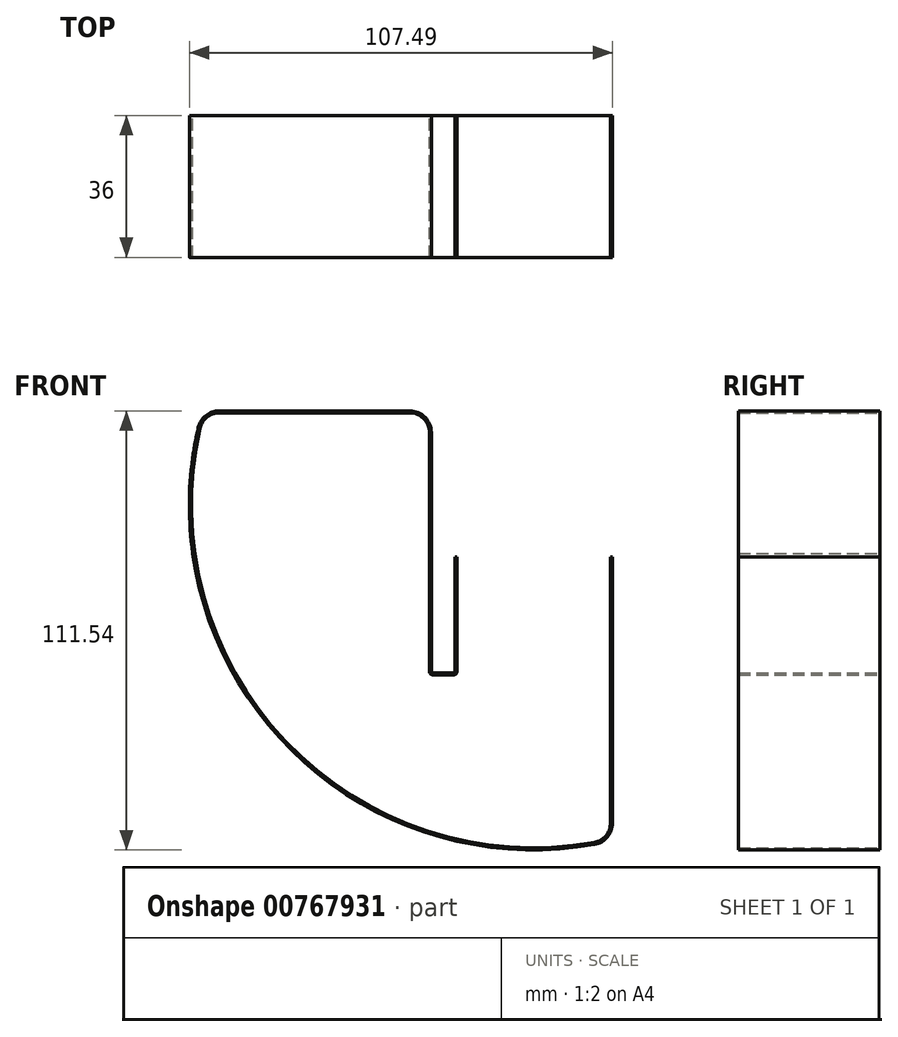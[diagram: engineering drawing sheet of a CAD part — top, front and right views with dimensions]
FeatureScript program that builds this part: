
annotation { "Feature Type Name" : "Feature", "Feature Type Description" : "" }
export const myFeature = defineFeature(function(context is Context, id is Id, definition is map)
    precondition{}
    {
        {
            var Q0;
            Q0=qCreatedBy(makeId("Front.planeOp"),FACE);
            var sketch = newSketch(context, id + "F0", { "sketchPlane" : qUnion([Q0])});
            skLineSegment(sketch, "E0", {"start": v(19.5, -13.15) * mm, "end": v(20, -13.15) * mm});
            skLineSegment(sketch, "E1", {"start": v(-19.5, -13.15) * mm, "end": v(-20, -13.15) * mm});
            skLineSegment(sketch, "E2", {"start": v(-20, -13.15) * mm, "end": v(-20, -23.15) * mm});
            skLineSegment(sketch, "E3.0", {"start": v(-31.5, 23.5) * mm, "end": v(-50.68, 23.5) * mm});
            skArc(sketch, "E4", {"start": v(-85.23, 19.74) * mm, "mid": v(-86.02, 15.96) * mm, "end": v(-86.64, 12.14) * mm});
            skLineSegment(sketch, "E5", {"start": v(-31.5, 24) * mm, "end": v(-50.68, 24) * mm});
            skArc(sketch, "E6.0", {"start": v(-84.74, 19.63) * mm, "mid": v(-85.53, 15.87) * mm, "end": v(-86.14, 12.07) * mm});
            skLineSegment(sketch, "E7", {"start": v(20, -13.15) * mm, "end": v(20, -23.15) * mm});
            skLineSegment(sketch, "E8", {"start": v(-25.5, -42.65) * mm, "end": v(-20.5, -42.65) * mm});
            skLineSegment(sketch, "E9", {"start": v(-20.5, -43.15) * mm, "end": v(-25.5, -43.15) * mm});
            skLineSegment(sketch, "E10", {"start": v(-26.5, 18.5) * mm, "end": v(-26.5, 5) * mm});
            skLineSegment(sketch, "E11", {"start": v(-26, 18.5) * mm, "end": v(-26, 5) * mm});
            skPoint(sketch, "E12.visualSharp", {"position": v(19.5, -84.82) * mm});
            skArc(sketch, "E12.filletArc", {"start": v(15.38, -85.67) * mm, "mid": v(18.34, -83.95) * mm, "end": v(19.5, -80.74) * mm});
            skPoint(sketch, "E13.visualSharp", {"position": v(20, -85.22) * mm});
            skArc(sketch, "E13.filletArc", {"start": v(15.47, -86.16) * mm, "mid": v(18.72, -84.27) * mm, "end": v(20, -80.74) * mm});
            skPoint(sketch, "E14.visualSharp", {"position": v(-83.75, 23.5) * mm});
            skArc(sketch, "E14.filletArc", {"start": v(-79.87, 23.5) * mm, "mid": v(-82.98, 22.41) * mm, "end": v(-84.74, 19.63) * mm});
            skPoint(sketch, "E15.visualSharp", {"position": v(-84.13, 24) * mm});
            skArc(sketch, "E15.filletArc", {"start": v(-79.87, 24) * mm, "mid": v(-83.3, 22.8) * mm, "end": v(-85.23, 19.74) * mm});
            skPoint(sketch, "E16.visualSharp", {"position": v(-26.5, 23.5) * mm});
            skArc(sketch, "E16.filletArc", {"start": v(-26.5, 18.5) * mm, "mid": v(-27.96, 22.04) * mm, "end": v(-31.5, 23.5) * mm});
            skArc(sketch, "E17.filletArc", {"start": v(-26, 18.5) * mm, "mid": v(-27.61, 22.39) * mm, "end": v(-31.5, 24) * mm});
            skPoint(sketch, "E18.visualSharp", {"position": v(-26, -42.65) * mm});
            skArc(sketch, "E18.filletArc", {"start": v(-26, -42.15) * mm, "mid": v(-25.85, -42.5) * mm, "end": v(-25.5, -42.65) * mm});
            skPoint(sketch, "E19.visualSharp", {"position": v(-20, -42.65) * mm});
            skArc(sketch, "E19.filletArc", {"start": v(-20.5, -42.65) * mm, "mid": v(-20.15, -42.5) * mm, "end": v(-20, -42.15) * mm});
            skPoint(sketch, "E20.visualSharp", {"position": v(-19.5, -43.15) * mm});
            skArc(sketch, "E20.filletArc", {"start": v(-20.5, -43.15) * mm, "mid": v(-19.8, -42.86) * mm, "end": v(-19.5, -42.15) * mm});
            skPoint(sketch, "E21.visualSharp", {"position": v(-26.5, -43.15) * mm});
            skArc(sketch, "E21.filletArc", {"start": v(-26.5, -42.15) * mm, "mid": v(-26.2, -42.86) * mm, "end": v(-25.5, -43.15) * mm});
            skLineSegment(sketch, "E22.direction2", {"start": v(19.5, -42.15) * mm, "end": v(19.5, -58.15) * mm, "construction": true});
            skLineSegment(sketch, "E23.trimOffspring", {"start": v(20, -33.15) * mm, "end": v(20, -58.15) * mm});
            skLineSegment(sketch, "E24.trimOffspring", {"start": v(19.5, -42.15) * mm, "end": v(19.5, -58.15) * mm});
            skLineSegment(sketch, "E25.trimOffspring", {"start": v(20, -68.15) * mm, "end": v(20, -80.74) * mm});
            skLineSegment(sketch, "E26.trimOffspring", {"start": v(19.5, -68.15) * mm, "end": v(19.5, -80.74) * mm});
            skLineSegment(sketch, "E27.trimOffspring", {"start": v(-20, -33.15) * mm, "end": v(-20, -42.15) * mm});
            skLineSegment(sketch, "E28.trimOffspring", {"start": v(-26, -33.15) * mm, "end": v(-26, -42.15) * mm});
            skLineSegment(sketch, "E29.trimOffspring", {"start": v(-26.5, -33.15) * mm, "end": v(-26.5, -42.15) * mm});
            skLineSegment(sketch, "E30.trimOffspring", {"start": v(-26, -5) * mm, "end": v(-26, -23.15) * mm});
            skLineSegment(sketch, "E31.trimOffspring", {"start": v(-26.5, -5) * mm, "end": v(-26.5, -23.15) * mm});
            skLineSegment(sketch, "E32.trimOffspring", {"start": v(-60.68, 23.5) * mm, "end": v(-79.87, 23.5) * mm});
            skLineSegment(sketch, "E33.trimOffspring", {"start": v(-60.68, 24) * mm, "end": v(-79.87, 24) * mm});
            skLineSegment(sketch, "E34.1.1", {"start": v(-86.63, -12.2) * mm, "end": v(-86.64, -12.2) * mm});
            skArc(sketch, "E35.trimOffspring", {"start": v(-52.35, -69.52) * mm, "mid": v(-33.28, -80.42) * mm, "end": v(-12.08, -86.2) * mm});
            skArc(sketch, "E36.trimOffspring", {"start": v(-52.65, -69.92) * mm, "mid": v(-33.47, -80.88) * mm, "end": v(-12.15, -86.69) * mm});
            skArc(sketch, "E37.trimOffspring", {"start": v(12.14, -86.19) * mm, "mid": v(13.76, -85.94) * mm, "end": v(15.38, -85.67) * mm});
            skArc(sketch, "E38.trimOffspring", {"start": v(12.21, -86.68) * mm, "mid": v(13.84, -86.43) * mm, "end": v(15.47, -86.16) * mm});
            skArc(sketch, "E39.trimOffspring", {"start": v(-86.64, -12.2) * mm, "mid": v(-80.83, -33.52) * mm, "end": v(-69.87, -52.7) * mm});
            skArc(sketch, "E40.trimOffspring", {"start": v(-86.15, -12.14) * mm, "mid": v(-80.37, -33.33) * mm, "end": v(-69.47, -52.4) * mm});
            skLineSegment(sketch, "E41", {"start": v(19.5, -33.15) * mm, "end": v(19.5, -23.15) * mm});
            skLineSegment(sketch, "E42", {"start": v(-19.5, -33.15) * mm, "end": v(-19.5, -23.15) * mm});
            skArc(sketch, "E43", {"start": v(-86.64, 12.14) * mm, "mid": v(-87.49, -0.03) * mm, "end": v(-86.63, -12.2) * mm});
            skArc(sketch, "E44", {"start": v(-69.87, -52.7) * mm, "mid": v(-61.86, -61.9) * mm, "end": v(-52.65, -69.92) * mm});
            skArc(sketch, "E45", {"start": v(12.21, -86.68) * mm, "mid": v(0.03, -87.54) * mm, "end": v(-12.15, -86.69) * mm});
            skArc(sketch, "E46", {"start": v(-12.08, -86.2) * mm, "mid": v(0.03, -87.04) * mm, "end": v(12.14, -86.19) * mm});
            skArc(sketch, "E47", {"start": v(-52.35, -69.52) * mm, "mid": v(-61.5, -61.55) * mm, "end": v(-69.47, -52.4) * mm});
            skArc(sketch, "E48", {"start": v(-86.15, -12.14) * mm, "mid": v(-87, -0.03) * mm, "end": v(-86.14, 12.07) * mm});
            skLineSegment(sketch, "E49", {"start": v(-60.68, 24) * mm, "end": v(-50.68, 24) * mm});
            skLineSegment(sketch, "E50", {"start": v(-50.68, 23.5) * mm, "end": v(-60.68, 23.5) * mm});
            skLineSegment(sketch, "E51", {"start": v(-26.5, 5) * mm, "end": v(-26.5, -5) * mm});
            skLineSegment(sketch, "E52", {"start": v(-26, -5) * mm, "end": v(-26, 5) * mm});
            skLineSegment(sketch, "E53", {"start": v(-26.5, -33.15) * mm, "end": v(-26.5, -23.15) * mm});
            skLineSegment(sketch, "E54", {"start": v(-26, -23.15) * mm, "end": v(-26, -33.15) * mm});
            skLineSegment(sketch, "E55", {"start": v(-19.5, -42.15) * mm, "end": v(-19.5, -33.15) * mm});
            skLineSegment(sketch, "E56", {"start": v(-20, -33.15) * mm, "end": v(-20, -23.15) * mm});
            skLineSegment(sketch, "E57", {"start": v(-19.5, -23.15) * mm, "end": v(-19.5, -13.15) * mm});
            skLineSegment(sketch, "E58", {"start": v(19.5, -23.15) * mm, "end": v(19.5, -13.15) * mm});
            skLineSegment(sketch, "E59", {"start": v(20, -23.15) * mm, "end": v(20, -33.15) * mm});
            skLineSegment(sketch, "E60", {"start": v(19.5, -42.15) * mm, "end": v(19.5, -33.15) * mm});
            skLineSegment(sketch, "E61", {"start": v(19.5, -68.15) * mm, "end": v(19.5, -58.15) * mm});
            skLineSegment(sketch, "E62", {"start": v(20, -58.15) * mm, "end": v(20, -68.15) * mm});
            skSolve(sketch);
        }
        {
            var Q0;
            Q0=makeQuery(id+"F0.imprint","IMPRINT",FACE,{"disambiguationData":[TD([[makeQuery(id+"F0.imprint","IMPRINT",EDGE,{"derivedFrom":sQuery(id+"F0.wireOp",EDGE,"E0")}),-1.0]])]});
            extrude(context, id + "F1", {"entities" : qUnion([Q0]), "depth" : 36 * mm, "offsetDistance" : 25 * mm});
        }
    });
